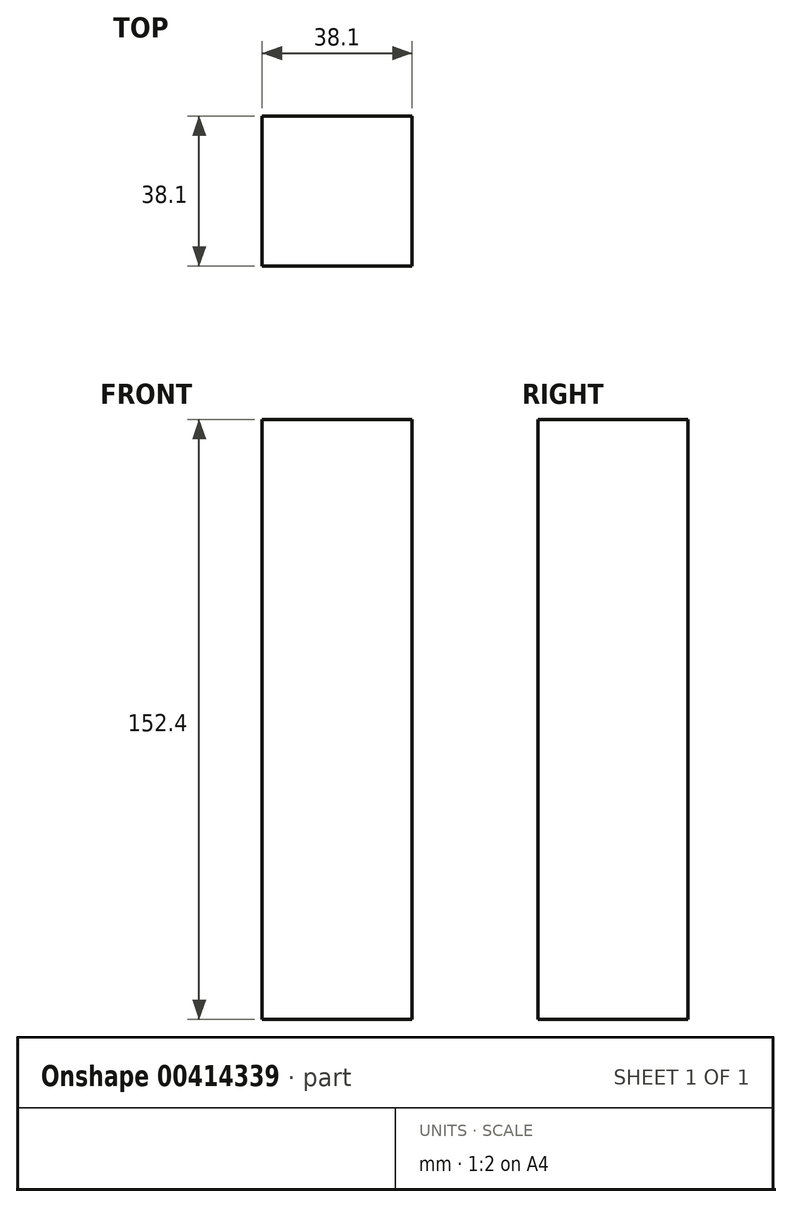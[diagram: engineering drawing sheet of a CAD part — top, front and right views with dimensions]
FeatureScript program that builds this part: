
annotation { "Feature Type Name" : "Feature", "Feature Type Description" : "" }
export const myFeature = defineFeature(function(context is Context, id is Id, definition is map)
    precondition{}
    {
        {
            var Q0;
            Q0=qCreatedBy(makeId("Top.planeOp"),FACE);
            var sketch = newSketch(context, id + "F0", { "sketchPlane" : qUnion([Q0])});
            skLineSegment(sketch, "E0.bottom", {"start": v(-19.05, 19.05) * mm, "end": v(19.05, 19.05) * mm});
            skLineSegment(sketch, "E0.top", {"start": v(-19.05, -19.05) * mm, "end": v(19.05, -19.05) * mm});
            skLineSegment(sketch, "E0.left", {"start": v(-19.05, 19.05) * mm, "end": v(-19.05, -19.05) * mm});
            skLineSegment(sketch, "E0.right", {"start": v(19.05, 19.05) * mm, "end": v(19.05, -19.05) * mm});
            skPoint(sketch, "E0.middle", {"position": v(0, 0) * mm});
            skSolve(sketch);
        }
        {
            var Q0;
            Q0 = qSketchRegion(id + "F0", true);
            extrude(context, id + "F1", {"entities" : qUnion([Q0]), "depth" : 152.4 * mm});
        }
    });
